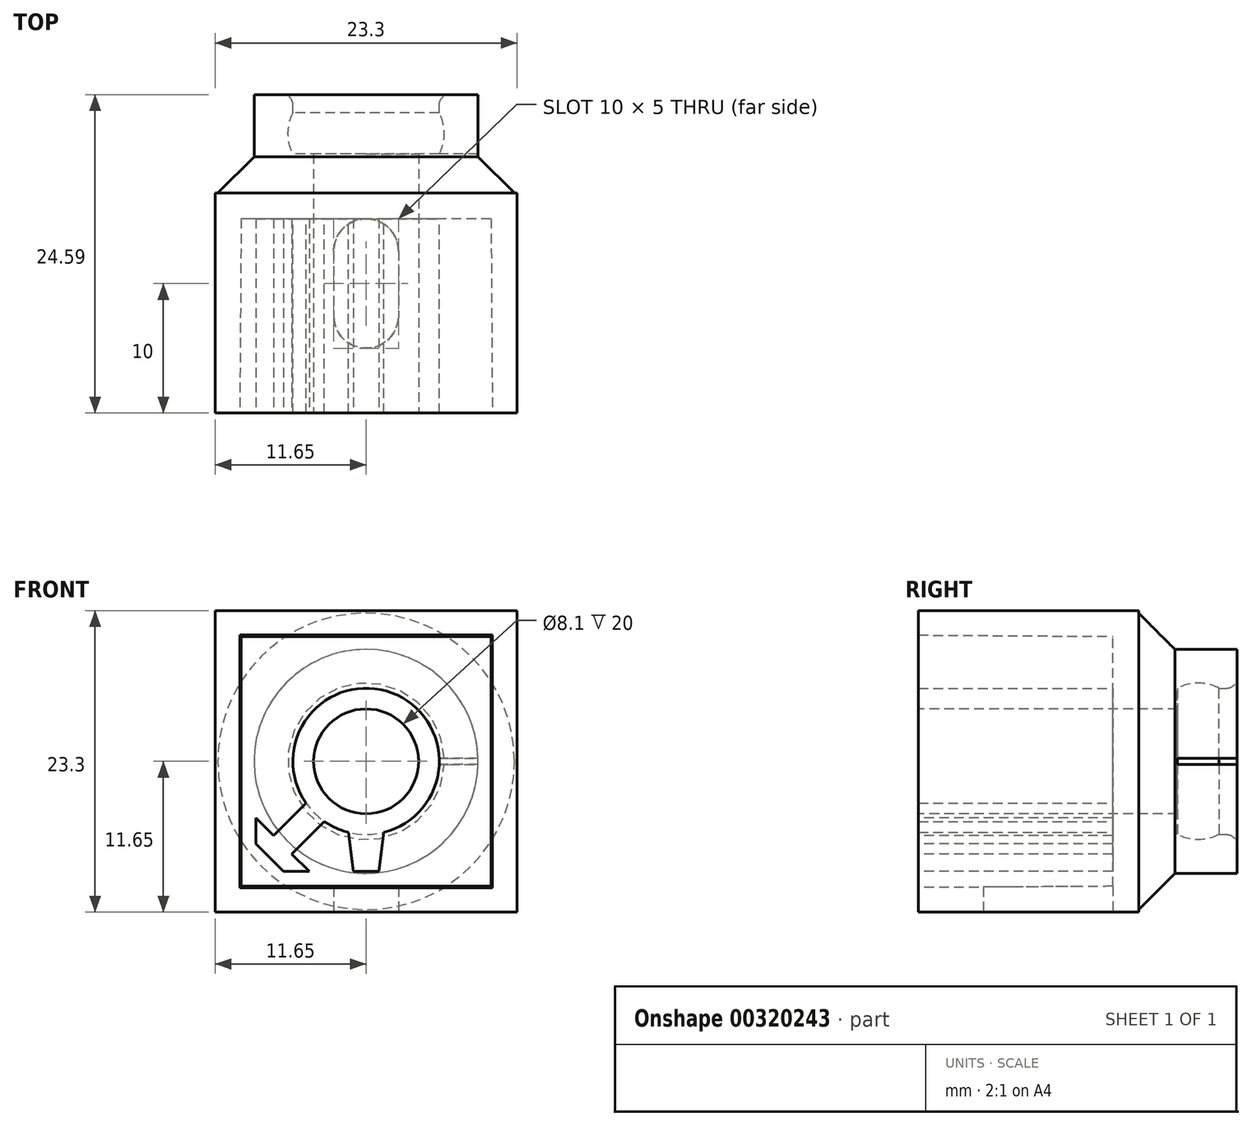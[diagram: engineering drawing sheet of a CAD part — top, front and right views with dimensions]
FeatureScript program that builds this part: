
annotation { "Feature Type Name" : "Feature", "Feature Type Description" : "" }
export const myFeature = defineFeature(function(context is Context, id is Id, definition is map)
    precondition{}
    {
        {
            var Q0;
            Q0=qCreatedBy(makeId("Front.planeOp"),FACE);
            var sketch = newSketch(context, id + "F0", { "sketchPlane" : qUnion([Q0])});
            skLineSegment(sketch, "E0.bottom", {"start": v(9.5, -9.5) * mm, "end": v(-9.5, -9.5) * mm, "construction": true});
            skLineSegment(sketch, "E0.top", {"start": v(9.5, 9.5) * mm, "end": v(-9.5, 9.5) * mm, "construction": true});
            skLineSegment(sketch, "E0.left", {"start": v(9.5, -9.5) * mm, "end": v(9.5, 9.5) * mm, "construction": true});
            skLineSegment(sketch, "E0.right", {"start": v(-9.5, -9.5) * mm, "end": v(-9.5, 9.5) * mm, "construction": true});
            skPoint(sketch, "E0.middle", {"position": v(0, 0) * mm});
            skLineSegment(sketch, "E1.0", {"start": v(8.5, 8.5) * mm, "end": v(-8.5, 8.5) * mm, "construction": true});
            skLineSegment(sketch, "E1.1", {"start": v(8.5, -8.5) * mm, "end": v(8.5, 8.5) * mm, "construction": true});
            skLineSegment(sketch, "E1.2", {"start": v(8.5, -8.5) * mm, "end": v(-8.5, -8.5) * mm, "construction": true});
            skLineSegment(sketch, "E1.3", {"start": v(-8.5, -8.5) * mm, "end": v(-8.5, 8.5) * mm, "construction": true});
            skSolve(sketch);
        }
        {
            var Q0;
            Q0=qCreatedBy(makeId("Front.planeOp"),FACE);
            var sketch = newSketch(context, id + "F1", { "sketchPlane" : qUnion([Q0])});
            skLineSegment(sketch, "E2.0", {"start": v(8.4, 8.4) * mm, "end": v(-8.4, 8.4) * mm});
            skLineSegment(sketch, "E2.1", {"start": v(8.4, -8.4) * mm, "end": v(8.4, 8.4) * mm});
            skLineSegment(sketch, "E2.2", {"start": v(8.4, -8.4) * mm, "end": v(-8.4, -8.4) * mm});
            skLineSegment(sketch, "E2.3", {"start": v(-8.4, -8.4) * mm, "end": v(-8.4, 8.4) * mm});
            skLineSegment(sketch, "E3.0", {"start": v(9.65, 9.65) * mm, "end": v(-9.65, 9.65) * mm});
            skLineSegment(sketch, "E3.1", {"start": v(9.65, -9.65) * mm, "end": v(9.65, 9.65) * mm});
            skLineSegment(sketch, "E3.2", {"start": v(9.65, -9.65) * mm, "end": v(-9.65, -9.65) * mm});
            skLineSegment(sketch, "E3.3", {"start": v(-9.65, -9.65) * mm, "end": v(-9.65, 9.65) * mm});
            skLineSegment(sketch, "E4.0", {"start": v(11.65, 11.65) * mm, "end": v(-11.65, 11.65) * mm});
            skLineSegment(sketch, "E4.1", {"start": v(11.65, -11.65) * mm, "end": v(11.65, 11.65) * mm});
            skLineSegment(sketch, "E4.2", {"start": v(11.65, -11.65) * mm, "end": v(-11.65, -11.65) * mm});
            skLineSegment(sketch, "E4.3", {"start": v(-11.65, -11.65) * mm, "end": v(-11.65, 11.65) * mm});
            skLineSegment(sketch, "E5.0", {"start": v(6.4, 6.4) * mm, "end": v(-6.4, 6.4) * mm});
            skLineSegment(sketch, "E5.1", {"start": v(6.4, -6.4) * mm, "end": v(6.4, 6.4) * mm});
            skLineSegment(sketch, "E5.2", {"start": v(6.4, -6.4) * mm, "end": v(-6.4, -6.4) * mm});
            skLineSegment(sketch, "E5.3", {"start": v(-6.4, -6.4) * mm, "end": v(-6.4, 6.4) * mm});
            skSolve(sketch);
        }
        {
            var Q0;
            Q0=makeQuery(id+"F1.imprint","IMPRINT",FACE,{"disambiguationData":[TD([[makeQuery(id+"F1.imprint","IMPRINT",EDGE,{"derivedFrom":sQuery(id+"F1.wireOp",EDGE,"E3.0")}),-1.0]])]});
            extrude(context, id + "F2", {"entities" : qUnion([Q0]), "oppositeDirection" : true, "depth" : 25 * mm});
        }
        {
            var Q0;
            Q0=makeQuery(id+"F2.opExtrude","CAP_FACE",FACE,{"disambiguationData":[OSD([sQuery(id+"F1.wireOp",EDGE,"E3.0"),sQuery(id+"F1.wireOp",EDGE,"E3.1"),sQuery(id+"F1.wireOp",EDGE,"E3.2"),sQuery(id+"F1.wireOp",EDGE,"E3.3"),sQuery(id+"F1.wireOp",EDGE,"E4.0"),sQuery(id+"F1.wireOp",EDGE,"E4.1"),sQuery(id+"F1.wireOp",EDGE,"E4.2"),sQuery(id+"F1.wireOp",EDGE,"E4.3")])],"isStart":true});
            var sketch = newSketch(context, id + "F3", { "sketchPlane" : qUnion([Q0])});
            skLineSegment(sketch, "E6.0.0", {"start": v(-11.65, 11.65) * mm, "end": v(-11.65, -11.65) * mm});
            skLineSegment(sketch, "E6.0.1", {"start": v(-11.65, -11.65) * mm, "end": v(11.65, -11.65) * mm});
            skLineSegment(sketch, "E6.0.2", {"start": v(11.65, -11.65) * mm, "end": v(11.65, 11.65) * mm});
            skLineSegment(sketch, "E6.0.3", {"start": v(11.65, 11.65) * mm, "end": v(-11.65, 11.65) * mm});
            skSolve(sketch);
        }
        {
            var Q0;
            Q0 = qSketchRegion(id + "F3", true);
            extrude(context, id + "F4", {"entities" : qUnion([Q0]), "operationType" : NewBodyOperationType.ADD, "oppositeDirection" : true, "depth" : 3 * mm});
        }
        {
            var Q0;
            Q0=makeQuery(id+"F4.boolean.opBoolean","MERGE",FACE,{"derivedFrom":[makeQuery(id+"F2.opExtrude","CAP_FACE",FACE,{"disambiguationData":[OSD([sQuery(id+"F1.wireOp",EDGE,"E2.0"),sQuery(id+"F1.wireOp",EDGE,"E2.1"),sQuery(id+"F1.wireOp",EDGE,"E2.2"),sQuery(id+"F1.wireOp",EDGE,"E2.3"),sQuery(id+"F1.wireOp",EDGE,"E5.0"),sQuery(id+"F1.wireOp",EDGE,"E5.1"),sQuery(id+"F1.wireOp",EDGE,"E5.2"),sQuery(id+"F1.wireOp",EDGE,"E5.3")])],"isStart":true}),makeQuery(id+"F2.opExtrude","CAP_FACE",FACE,{"disambiguationData":[OSD([sQuery(id+"F1.wireOp",EDGE,"E3.0"),sQuery(id+"F1.wireOp",EDGE,"E3.1"),sQuery(id+"F1.wireOp",EDGE,"E3.2"),sQuery(id+"F1.wireOp",EDGE,"E3.3"),sQuery(id+"F1.wireOp",EDGE,"E4.0"),sQuery(id+"F1.wireOp",EDGE,"E4.1"),sQuery(id+"F1.wireOp",EDGE,"E4.2"),sQuery(id+"F1.wireOp",EDGE,"E4.3")])],"isStart":true}),makeQuery(id+"F4.opExtrude","CAP_FACE",FACE,{"disambiguationData":[OSD([sQuery(id+"F3.wireOp",EDGE,"E6.0.0"),sQuery(id+"F3.wireOp",EDGE,"E6.0.1"),sQuery(id+"F3.wireOp",EDGE,"E6.0.2"),sQuery(id+"F3.wireOp",EDGE,"E6.0.3")])],"isStart":true})]});
            var sketch = newSketch(context, id + "F5", { "sketchPlane" : qUnion([Q0])});
            skCircle(sketch, "E7", {"center": v(0, 0) * mm, "radius": 4.05 * mm});
            skSolve(sketch);
        }
        {
            var Q0;
            Q0 = qSketchRegion(id + "F5", true);
            extrude(context, id + "F6", {"entities" : qUnion([Q0]), "operationType" : NewBodyOperationType.REMOVE, "endBound" : BoundingType.THROUGH_ALL, "oppositeDirection" : true, "depth" : 25 * mm});
        }
        {
            var Q0;
            Q0=qCreatedBy(makeId("Right.planeOp"),FACE);
            var sketch = newSketch(context, id + "F7", { "sketchPlane" : qUnion([Q0])});
            skLineSegment(sketch, "E8.bottom", {"start": v(3, -4.05) * mm, "end": v(20, -4.05) * mm});
            skLineSegment(sketch, "E8.top", {"start": v(3, -5.65) * mm, "end": v(20, -5.65) * mm});
            skLineSegment(sketch, "E8.left", {"start": v(3, -4.05) * mm, "end": v(3, -5.65) * mm});
            skLineSegment(sketch, "E8.right", {"start": v(20, -4.05) * mm, "end": v(20, -5.65) * mm});
            skArc(sketch, "E9", {"start": v(20, -5.65) * mm, "mid": v(21.6, -6.05) * mm, "end": v(23.2, -5.65) * mm});
            skLineSegment(sketch, "E10", {"start": v(23.2, -5.65) * mm, "end": v(26.09, -5.65) * mm});
            skArc(sketch, "E11.0", {"start": v(17.11, -5.65) * mm, "mid": v(21.6, -8.05) * mm, "end": v(26.09, -5.65) * mm});
            skLineSegment(sketch, "E12", {"start": v(24.82, -8.05) * mm, "end": v(16.07, -8.05) * mm, "construction": true});
            skSolve(sketch);
        }
        {
            var Q0;
            Q0 = qSketchRegion(id + "F7", true);
            var Q1;
            Q1=makeQuery(id+"F6.boolean.opBoolean","INTERSECT",EDGE,{"derivedFrom":[makeQuery(id+"F4.opExtrude","CAP_FACE",FACE,{"disambiguationData":[OSD([sQuery(id+"F3.wireOp",EDGE,"E6.0.0"),sQuery(id+"F3.wireOp",EDGE,"E6.0.1"),sQuery(id+"F3.wireOp",EDGE,"E6.0.2"),sQuery(id+"F3.wireOp",EDGE,"E6.0.3")])],"isStart":false}),makeQuery(id+"F6.opExtrude","SWEPT_FACE",FACE,{"disambiguationData":[OSD([sQuery(id+"F5.wireOp",EDGE,"E7")])]})]});
            revolve(context, id + "F8", {"operationType" : NewBodyOperationType.ADD, "entities" : qUnion([Q0]), "axis" : qUnion([Q1]), "revolveType" : RevolveType.FULL});
        }
        {
            var Q0;
            Q0=makeQuery(id+"F2.opExtrude","CAP_FACE",FACE,{"disambiguationData":[OSD([sQuery(id+"F1.wireOp",EDGE,"E3.0"),sQuery(id+"F1.wireOp",EDGE,"E3.1"),sQuery(id+"F1.wireOp",EDGE,"E3.2"),sQuery(id+"F1.wireOp",EDGE,"E3.3"),sQuery(id+"F1.wireOp",EDGE,"E4.0"),sQuery(id+"F1.wireOp",EDGE,"E4.1"),sQuery(id+"F1.wireOp",EDGE,"E4.2"),sQuery(id+"F1.wireOp",EDGE,"E4.3")])],"isStart":false});
            cPlane(context, id + "F9", {"entities" : qUnion([Q0]), "cplaneType" : CPlaneType.OFFSET, "offset" : 8 * mm, "oppositeDirection" : true, "width" : 150 * mm, "height" : 150 * mm});
        }
        {
            var Q0;
            Q0=qCreatedBy(id+"F9.planeOp",FACE);
            var sketch = newSketch(context, id + "F10", { "sketchPlane" : qUnion([Q0])});
            skLineSegment(sketch, "E13.0.0", {"start": v(11.65, -11.65) * mm, "end": v(11.65, 11.65) * mm});
            skLineSegment(sketch, "E13.0.1", {"start": v(11.65, 11.65) * mm, "end": v(-11.65, 11.65) * mm});
            skLineSegment(sketch, "E13.0.2", {"start": v(-11.65, 11.65) * mm, "end": v(-11.65, -11.65) * mm});
            skLineSegment(sketch, "E13.0.3", {"start": v(-11.65, -11.65) * mm, "end": v(11.65, -11.65) * mm});
            skSolve(sketch);
        }
        {
            var Q0;
            Q0 = qSketchRegion(id + "F10", true);
            extrude(context, id + "F11", {"entities" : qUnion([Q0]), "oppositeDirection" : true, "depth" : 2 * mm});
        }
        {
            var Q0;
            Q0=makeQuery(id+"F2.opExtrude","SWEPT_BODY",BODY,{"disambiguationData":[OSD([sQuery(id+"F1.wireOp",EDGE,"E3.0"),sQuery(id+"F1.wireOp",EDGE,"E3.1"),sQuery(id+"F1.wireOp",EDGE,"E3.2"),sQuery(id+"F1.wireOp",EDGE,"E3.3"),sQuery(id+"F1.wireOp",EDGE,"E4.0"),sQuery(id+"F1.wireOp",EDGE,"E4.1"),sQuery(id+"F1.wireOp",EDGE,"E4.2"),sQuery(id+"F1.wireOp",EDGE,"E4.3")])]});
            var Q1;
            Q1=makeQuery(id+"F11.opExtrude","SWEPT_BODY",BODY,{"disambiguationData":[OSD([sQuery(id+"F10.wireOp",EDGE,"E13.0.0"),sQuery(id+"F10.wireOp",EDGE,"E13.0.1"),sQuery(id+"F10.wireOp",EDGE,"E13.0.2"),sQuery(id+"F10.wireOp",EDGE,"E13.0.3")])]});
            booleanBodies(context, id + "F12", {"operationType" : BooleanOperationType.UNION, "tools" : qUnion([Q0, Q1])});
        }
        {
            var Q0;
            Q0=makeQuery(id+"F12.opBoolean","SPLIT",FACE,{"disambiguationData":[TD([makeQuery(id+"F6.boolean.opBoolean","COPY",FACE,{"derivedFrom":makeQuery(id+"F6.opExtrude","SWEPT_FACE",FACE,{"disambiguationData":[OSD([sQuery(id+"F5.wireOp",EDGE,"E7")])]})})])],"derivedFrom":makeQuery(id+"F11.opExtrude","CAP_FACE",FACE,{"disambiguationData":[OSD([sQuery(id+"F10.wireOp",EDGE,"E13.0.0"),sQuery(id+"F10.wireOp",EDGE,"E13.0.1"),sQuery(id+"F10.wireOp",EDGE,"E13.0.2"),sQuery(id+"F10.wireOp",EDGE,"E13.0.3")])],"isStart":true})});
            var sketch = newSketch(context, id + "F13", { "sketchPlane" : qUnion([Q0])});
            skCircle(sketch, "E14.0", {"center": v(0, 0) * mm, "radius": 4.05 * mm});
            skSolve(sketch);
        }
        {
            var Q0;
            Q0 = qSketchRegion(id + "F13", true);
            extrude(context, id + "F14", {"entities" : qUnion([Q0]), "operationType" : NewBodyOperationType.REMOVE, "endBound" : BoundingType.THROUGH_ALL, "oppositeDirection" : true, "depth" : 25 * mm});
        }
        {
            var Q0;
            Q0=makeQuery(id+"F4.opExtrude","CAP_FACE",FACE,{"disambiguationData":[OSD([sQuery(id+"F3.wireOp",EDGE,"E6.0.0"),sQuery(id+"F3.wireOp",EDGE,"E6.0.1"),sQuery(id+"F3.wireOp",EDGE,"E6.0.2"),sQuery(id+"F3.wireOp",EDGE,"E6.0.3")])],"isStart":false});
            var sketch = newSketch(context, id + "F15", { "sketchPlane" : qUnion([Q0])});
            skLineSegment(sketch, "E15.0.0", {"start": v(-9.65, -9.65) * mm, "end": v(9.65, -9.65) * mm});
            skLineSegment(sketch, "E15.0.1", {"start": v(9.65, -9.65) * mm, "end": v(9.65, 9.65) * mm});
            skLineSegment(sketch, "E15.0.2", {"start": v(9.65, 9.65) * mm, "end": v(-9.65, 9.65) * mm});
            skLineSegment(sketch, "E15.0.3", {"start": v(-9.65, 9.65) * mm, "end": v(-9.65, -9.65) * mm});
            skCircle(sketch, "E16.0", {"center": v(0, 0) * mm, "radius": 5.65 * mm});
            skSolve(sketch);
        }
        {
            var Q0;
            Q0 = qSketchRegion(id + "F15", true);
            extrude(context, id + "F16", {"entities" : qUnion([Q0]), "operationType" : NewBodyOperationType.REMOVE, "endBound" : BoundingType.THROUGH_ALL, "oppositeDirection" : true, "depth" : 25 * mm});
        }
        {
            var Q0;
            Q0=makeQuery(id+"F12.opBoolean","SPLIT",FACE,{"disambiguationData":[TD([makeQuery(id+"F2.opExtrude","SWEPT_FACE",FACE,{"disambiguationData":[OSD([sQuery(id+"F1.wireOp",EDGE,"E3.0")])]})])],"derivedFrom":makeQuery(id+"F11.opExtrude","CAP_FACE",FACE,{"disambiguationData":[OSD([sQuery(id+"F10.wireOp",EDGE,"E13.0.0"),sQuery(id+"F10.wireOp",EDGE,"E13.0.1"),sQuery(id+"F10.wireOp",EDGE,"E13.0.2"),sQuery(id+"F10.wireOp",EDGE,"E13.0.3")])],"isStart":false})});
            var sketch = newSketch(context, id + "F17", { "sketchPlane" : qUnion([Q0])});
            skLineSegment(sketch, "E17.0", {"start": v(9.5, -9.5) * mm, "end": v(-9.5, -9.5) * mm});
            skLineSegment(sketch, "E17.1", {"start": v(9.5, 9.5) * mm, "end": v(-9.5, 9.5) * mm});
            skLineSegment(sketch, "E17.2", {"start": v(9.5, -9.5) * mm, "end": v(9.5, 9.5) * mm});
            skLineSegment(sketch, "E17.3", {"start": v(-9.5, -9.5) * mm, "end": v(-9.5, 9.5) * mm});
            skPoint(sketch, "E17.4", {"position": v(0, 0) * mm});
            skLineSegment(sketch, "E17.5", {"start": v(8.5, 8.5) * mm, "end": v(-8.5, 8.5) * mm});
            skLineSegment(sketch, "E17.6", {"start": v(8.5, -8.5) * mm, "end": v(8.5, 8.5) * mm});
            skLineSegment(sketch, "E17.7", {"start": v(8.5, -8.5) * mm, "end": v(-8.5, -8.5) * mm});
            skLineSegment(sketch, "E17.8", {"start": v(-8.5, -8.5) * mm, "end": v(-8.5, 8.5) * mm});
            skSolve(sketch);
        }
        {
            var Q0;
            {var subQ0=sQuery(id+"F1.wireOp",EDGE,"E4.3");var subQ1=sQuery(id+"F1.wireOp",EDGE,"E4.2");var subQ2=sQuery(id+"F1.wireOp",EDGE,"E4.1");var subQ3=sQuery(id+"F1.wireOp",EDGE,"E4.0");var subQ4=sQuery(id+"F1.wireOp",EDGE,"E3.0");var subQ5=sQuery(id+"F1.wireOp",EDGE,"E3.3");var subQ6=sQuery(id+"F1.wireOp",EDGE,"E3.1");var subQ7=sQuery(id+"F1.wireOp",EDGE,"E3.2");Q0=makeQuery(id+"F16.boolean.opBoolean","SPLIT",FACE,{"disambiguationData":[TD([makeQuery(id+"F2.opExtrude","SWEPT_FACE",FACE,{"disambiguationData":[OSD([subQ4])]})])],"derivedFrom":makeQuery(id+"F4.boolean.opBoolean","MERGE",FACE,{"derivedFrom":[makeQuery(id+"F2.opExtrude","CAP_FACE",FACE,{"disambiguationData":[OSD([subQ4,subQ6,subQ7,subQ5,subQ3,subQ2,subQ1,subQ0])],"isStart":true}),makeQuery(id+"F4.opExtrude","CAP_FACE",FACE,{"disambiguationData":[OSD([sQuery(id+"F3.wireOp",EDGE,"E6.0.0"),sQuery(id+"F3.wireOp",EDGE,"E6.0.1"),sQuery(id+"F3.wireOp",EDGE,"E6.0.2"),sQuery(id+"F3.wireOp",EDGE,"E6.0.3")])],"isStart":true})]})});}
            var sketch = newSketch(context, id + "F18", { "sketchPlane" : qUnion([Q0])});
            skLineSegment(sketch, "E18", {"start": v(1.5, -4.5) * mm, "end": v(0.97, -8.5) * mm});
            skLineSegment(sketch, "E19", {"start": v(-0.97, -8.5) * mm, "end": v(-1.5, -4.5) * mm});
            skLineSegment(sketch, "E20", {"start": v(-1.5, -4.5) * mm, "end": v(1.5, -4.5) * mm});
            skLineSegment(sketch, "E21.0", {"start": v(8.5, -8.5) * mm, "end": v(-8.5, -8.5) * mm, "construction": true});
            skPoint(sketch, "E22.orphan", {"position": v(0, -15.9) * mm});
            skLineSegment(sketch, "E23", {"start": v(-0.97, -8.5) * mm, "end": v(0.97, -8.5) * mm});
            skSolve(sketch);
        }
        {
            var Q0;
            Q0 = qSketchRegion(id + "F18", true);
            var Q1;
            Q1=makeQuery(id+"F12.opBoolean","SPLIT",FACE,{"disambiguationData":[TD([makeQuery(id+"F2.opExtrude","SWEPT_FACE",FACE,{"disambiguationData":[OSD([sQuery(id+"F1.wireOp",EDGE,"E3.0")])]})])],"derivedFrom":makeQuery(id+"F11.opExtrude","CAP_FACE",FACE,{"disambiguationData":[OSD([sQuery(id+"F10.wireOp",EDGE,"E13.0.0"),sQuery(id+"F10.wireOp",EDGE,"E13.0.1"),sQuery(id+"F10.wireOp",EDGE,"E13.0.2"),sQuery(id+"F10.wireOp",EDGE,"E13.0.3")])],"isStart":false})});
            extrude(context, id + "F19", {"entities" : qUnion([Q0]), "operationType" : NewBodyOperationType.ADD, "endBound" : BoundingType.UP_TO_SURFACE, "oppositeDirection" : true, "endBoundEntityFace" : qUnion([Q1]), "depth" : 25 * mm});
        }
        {
            var Q0;
            {var subQ0=sQuery(id+"F1.wireOp",EDGE,"E4.3");var subQ1=sQuery(id+"F1.wireOp",EDGE,"E4.2");var subQ2=sQuery(id+"F1.wireOp",EDGE,"E4.1");var subQ3=sQuery(id+"F1.wireOp",EDGE,"E4.0");var subQ4=sQuery(id+"F1.wireOp",EDGE,"E3.0");var subQ5=sQuery(id+"F1.wireOp",EDGE,"E3.3");var subQ6=sQuery(id+"F1.wireOp",EDGE,"E3.1");var subQ7=sQuery(id+"F1.wireOp",EDGE,"E3.2");Q0=makeQuery(id+"F16.boolean.opBoolean","SPLIT",FACE,{"disambiguationData":[TD([makeQuery(id+"F2.opExtrude","SWEPT_FACE",FACE,{"disambiguationData":[OSD([subQ4])]})])],"derivedFrom":makeQuery(id+"F4.boolean.opBoolean","MERGE",FACE,{"derivedFrom":[makeQuery(id+"F2.opExtrude","CAP_FACE",FACE,{"disambiguationData":[OSD([subQ4,subQ6,subQ7,subQ5,subQ3,subQ2,subQ1,subQ0])],"isStart":true}),makeQuery(id+"F4.opExtrude","CAP_FACE",FACE,{"disambiguationData":[OSD([sQuery(id+"F3.wireOp",EDGE,"E6.0.0"),sQuery(id+"F3.wireOp",EDGE,"E6.0.1"),sQuery(id+"F3.wireOp",EDGE,"E6.0.2"),sQuery(id+"F3.wireOp",EDGE,"E6.0.3")])],"isStart":true})]})});}
            var sketch = newSketch(context, id + "F20", { "sketchPlane" : qUnion([Q0])});
            skLineSegment(sketch, "E24", {"start": v(-6.38, -8.5) * mm, "end": v(-8.5, -6.38) * mm});
            skLineSegment(sketch, "E25.0", {"start": v(-8.5, -6.38) * mm, "end": v(-8.5, -4.38) * mm});
            skLineSegment(sketch, "E26.0", {"start": v(-4.38, -8.5) * mm, "end": v(-6.38, -8.5) * mm});
            skCircle(sketch, "E27.0", {"center": v(0, 0) * mm, "radius": 4.05 * mm});
            skPoint(sketch, "E28.orphan", {"position": v(-8.5, 8.5) * mm});
            skPoint(sketch, "E29.orphan", {"position": v(8.5, -8.5) * mm});
            skPoint(sketch, "E30.orphan", {"position": v(-8.5, -8.5) * mm});
            skLineSegment(sketch, "E31", {"start": v(-8.5, -4.38) * mm, "end": v(-4.38, -8.5) * mm});
            skLineSegment(sketch, "E32", {"start": v(-6.44, -6.44) * mm, "end": v(0, 0) * mm, "construction": true});
            skLineSegment(sketch, "E33.0", {"start": v(-5.73, -7.15) * mm, "end": v(-2.07, -3.48) * mm});
            skLineSegment(sketch, "E34.0", {"start": v(-7.15, -5.73) * mm, "end": v(-3.48, -2.07) * mm});
            skSolve(sketch);
        }
        {
            var Q0;
            Q0=makeQuery(id+"F20.imprint","IMPRINT",FACE,{"disambiguationData":[TD([[makeQuery(id+"F20.imprint","IMPRINT",EDGE,{"derivedFrom":sQuery(id+"F20.wireOp",EDGE,"E24")}),-1.0]])]});
            var Q1;
            {var subQ0=sQuery(id+"F20.wireOp",EDGE,"E33.0");Q1=makeQuery(id+"F20.imprint","IMPRINT",FACE,{"disambiguationData":[TD([[makeQuery(id+"F20.imprint","IMPRINT",EDGE,{"derivedFrom":subQ0}),1.0]])]});}
            var Q2;
            Q2=makeQuery(id+"F12.opBoolean","SPLIT",FACE,{"disambiguationData":[TD([makeQuery(id+"F2.opExtrude","SWEPT_FACE",FACE,{"disambiguationData":[OSD([sQuery(id+"F1.wireOp",EDGE,"E3.0")])]})])],"derivedFrom":makeQuery(id+"F11.opExtrude","CAP_FACE",FACE,{"disambiguationData":[OSD([sQuery(id+"F10.wireOp",EDGE,"E13.0.0"),sQuery(id+"F10.wireOp",EDGE,"E13.0.1"),sQuery(id+"F10.wireOp",EDGE,"E13.0.2"),sQuery(id+"F10.wireOp",EDGE,"E13.0.3")])],"isStart":false})});
            extrude(context, id + "F21", {"entities" : qUnion([Q0, Q1]), "operationType" : NewBodyOperationType.ADD, "endBound" : BoundingType.UP_TO_SURFACE, "oppositeDirection" : true, "endBoundEntityFace" : qUnion([Q2]), "depth" : 25 * mm});
        }
        {
            var Q0;
            Q0=makeQuery(id+"F16.boolean.opBoolean","INTERSECT",EDGE,{"derivedFrom":[makeQuery(id+"F4.boolean.opBoolean","MERGE",FACE,{"derivedFrom":[makeQuery(id+"F2.opExtrude","CAP_FACE",FACE,{"disambiguationData":[OSD([sQuery(id+"F1.wireOp",EDGE,"E3.0"),sQuery(id+"F1.wireOp",EDGE,"E3.1"),sQuery(id+"F1.wireOp",EDGE,"E3.2"),sQuery(id+"F1.wireOp",EDGE,"E3.3"),sQuery(id+"F1.wireOp",EDGE,"E4.0"),sQuery(id+"F1.wireOp",EDGE,"E4.1"),sQuery(id+"F1.wireOp",EDGE,"E4.2"),sQuery(id+"F1.wireOp",EDGE,"E4.3")])],"isStart":true}),makeQuery(id+"F4.opExtrude","CAP_FACE",FACE,{"disambiguationData":[OSD([sQuery(id+"F3.wireOp",EDGE,"E6.0.0"),sQuery(id+"F3.wireOp",EDGE,"E6.0.1"),sQuery(id+"F3.wireOp",EDGE,"E6.0.2"),sQuery(id+"F3.wireOp",EDGE,"E6.0.3")])],"isStart":true})]}),makeQuery(id+"F16.opExtrude","SWEPT_FACE",FACE,{"disambiguationData":[OSD([sQuery(id+"F15.wireOp",EDGE,"E15.0.0")])]})]});
            var Q1;
            Q1=makeQuery(id+"F16.boolean.opBoolean","INTERSECT",EDGE,{"derivedFrom":[makeQuery(id+"F4.boolean.opBoolean","MERGE",FACE,{"derivedFrom":[makeQuery(id+"F2.opExtrude","CAP_FACE",FACE,{"disambiguationData":[OSD([sQuery(id+"F1.wireOp",EDGE,"E3.0"),sQuery(id+"F1.wireOp",EDGE,"E3.1"),sQuery(id+"F1.wireOp",EDGE,"E3.2"),sQuery(id+"F1.wireOp",EDGE,"E3.3"),sQuery(id+"F1.wireOp",EDGE,"E4.0"),sQuery(id+"F1.wireOp",EDGE,"E4.1"),sQuery(id+"F1.wireOp",EDGE,"E4.2"),sQuery(id+"F1.wireOp",EDGE,"E4.3")])],"isStart":true}),makeQuery(id+"F4.opExtrude","CAP_FACE",FACE,{"disambiguationData":[OSD([sQuery(id+"F3.wireOp",EDGE,"E6.0.0"),sQuery(id+"F3.wireOp",EDGE,"E6.0.1"),sQuery(id+"F3.wireOp",EDGE,"E6.0.2"),sQuery(id+"F3.wireOp",EDGE,"E6.0.3")])],"isStart":true})]}),makeQuery(id+"F16.opExtrude","SWEPT_FACE",FACE,{"disambiguationData":[OSD([sQuery(id+"F15.wireOp",EDGE,"E15.0.3")])]})]});
            var Q2;
            Q2=makeQuery(id+"F16.boolean.opBoolean","INTERSECT",EDGE,{"derivedFrom":[makeQuery(id+"F4.boolean.opBoolean","MERGE",FACE,{"derivedFrom":[makeQuery(id+"F2.opExtrude","CAP_FACE",FACE,{"disambiguationData":[OSD([sQuery(id+"F1.wireOp",EDGE,"E3.0"),sQuery(id+"F1.wireOp",EDGE,"E3.1"),sQuery(id+"F1.wireOp",EDGE,"E3.2"),sQuery(id+"F1.wireOp",EDGE,"E3.3"),sQuery(id+"F1.wireOp",EDGE,"E4.0"),sQuery(id+"F1.wireOp",EDGE,"E4.1"),sQuery(id+"F1.wireOp",EDGE,"E4.2"),sQuery(id+"F1.wireOp",EDGE,"E4.3")])],"isStart":true}),makeQuery(id+"F4.opExtrude","CAP_FACE",FACE,{"disambiguationData":[OSD([sQuery(id+"F3.wireOp",EDGE,"E6.0.0"),sQuery(id+"F3.wireOp",EDGE,"E6.0.1"),sQuery(id+"F3.wireOp",EDGE,"E6.0.2"),sQuery(id+"F3.wireOp",EDGE,"E6.0.3")])],"isStart":true})]}),makeQuery(id+"F16.opExtrude","SWEPT_FACE",FACE,{"disambiguationData":[OSD([sQuery(id+"F15.wireOp",EDGE,"E15.0.1")])]})]});
            var Q3;
            Q3=makeQuery(id+"F16.boolean.opBoolean","INTERSECT",EDGE,{"derivedFrom":[makeQuery(id+"F4.boolean.opBoolean","MERGE",FACE,{"derivedFrom":[makeQuery(id+"F2.opExtrude","CAP_FACE",FACE,{"disambiguationData":[OSD([sQuery(id+"F1.wireOp",EDGE,"E3.0"),sQuery(id+"F1.wireOp",EDGE,"E3.1"),sQuery(id+"F1.wireOp",EDGE,"E3.2"),sQuery(id+"F1.wireOp",EDGE,"E3.3"),sQuery(id+"F1.wireOp",EDGE,"E4.0"),sQuery(id+"F1.wireOp",EDGE,"E4.1"),sQuery(id+"F1.wireOp",EDGE,"E4.2"),sQuery(id+"F1.wireOp",EDGE,"E4.3")])],"isStart":true}),makeQuery(id+"F4.opExtrude","CAP_FACE",FACE,{"disambiguationData":[OSD([sQuery(id+"F3.wireOp",EDGE,"E6.0.0"),sQuery(id+"F3.wireOp",EDGE,"E6.0.1"),sQuery(id+"F3.wireOp",EDGE,"E6.0.2"),sQuery(id+"F3.wireOp",EDGE,"E6.0.3")])],"isStart":true})]}),makeQuery(id+"F16.opExtrude","SWEPT_FACE",FACE,{"disambiguationData":[OSD([sQuery(id+"F15.wireOp",EDGE,"E15.0.2")])]})]});
            chamfer(context, id + "F22", {"entities" : qUnion([Q0, Q1, Q2, Q3]), "chamferType" : ChamferType.TWO_OFFSETS, "width1" : .1 * mm, "oppositeDirection" : false, "width2" : 15 * mm, "tangentPropagation" : true});
        }
        {
            var Q0;
            Q0=makeQuery(id+"F2.opExtrude","SWEPT_FACE",FACE,{"disambiguationData":[OSD([sQuery(id+"F1.wireOp",EDGE,"E4.2")])]});
            var sketch = newSketch(context, id + "F23", { "sketchPlane" : qUnion([Q0])});
            skLineSegment(sketch, "E35.bottom", {"start": v(2.5, -15) * mm, "end": v(-2.5, -15) * mm});
            skLineSegment(sketch, "E35.top", {"start": v(2.5, -5) * mm, "end": v(-2.5, -5) * mm});
            skLineSegment(sketch, "E35.left", {"start": v(2.5, -15) * mm, "end": v(2.5, -5) * mm});
            skLineSegment(sketch, "E35.right", {"start": v(-2.5, -15) * mm, "end": v(-2.5, -5) * mm});
            skPoint(sketch, "E35.middle", {"position": v(0, -10) * mm});
            skSolve(sketch);
        }
        {
            var Q0;
            Q0 = qSketchRegion(id + "F23", true);
            extrude(context, id + "F24", {"entities" : qUnion([Q0]), "operationType" : NewBodyOperationType.REMOVE, "oppositeDirection" : true, "depth" : 2.5 * mm});
        }
        {
            var Q0;
            Q0=makeQuery(id+"F24.boolean.opBoolean","COPY",EDGE,{"derivedFrom":makeQuery(id+"F24.opExtrude","SWEPT_EDGE",EDGE,{"disambiguationData":[OSD([sQuery(id+"F23.wireOp",EDGE,"E35.top"),sQuery(id+"F23.wireOp",EDGE,"E35.right")])]})});
            var Q1;
            Q1=makeQuery(id+"F24.boolean.opBoolean","COPY",EDGE,{"derivedFrom":makeQuery(id+"F24.opExtrude","SWEPT_EDGE",EDGE,{"disambiguationData":[OSD([sQuery(id+"F23.wireOp",EDGE,"E35.top"),sQuery(id+"F23.wireOp",EDGE,"E35.left")])]})});
            var Q2;
            Q2=makeQuery(id+"F24.boolean.opBoolean","COPY",EDGE,{"derivedFrom":makeQuery(id+"F24.opExtrude","SWEPT_EDGE",EDGE,{"disambiguationData":[OSD([sQuery(id+"F23.wireOp",EDGE,"E35.bottom"),sQuery(id+"F23.wireOp",EDGE,"E35.right")])]})});
            var Q3;
            Q3=makeQuery(id+"F24.boolean.opBoolean","COPY",EDGE,{"derivedFrom":makeQuery(id+"F24.opExtrude","SWEPT_EDGE",EDGE,{"disambiguationData":[OSD([sQuery(id+"F23.wireOp",EDGE,"E35.bottom"),sQuery(id+"F23.wireOp",EDGE,"E35.left")])]})});
            fillet(context, id + "F25", {"entities" : qUnion([Q0, Q1, Q2, Q3]), "radius" : 2.5 * mm, "tangentPropagation" : true, "allowEdgeOverflow" : false});
        }
        {
            var Q0;
            Q0=makeQuery(id+"F2.opExtrude","CAP_FACE",FACE,{"disambiguationData":[OSD([sQuery(id+"F1.wireOp",EDGE,"E3.0"),sQuery(id+"F1.wireOp",EDGE,"E3.1"),sQuery(id+"F1.wireOp",EDGE,"E3.2"),sQuery(id+"F1.wireOp",EDGE,"E3.3"),sQuery(id+"F1.wireOp",EDGE,"E4.0"),sQuery(id+"F1.wireOp",EDGE,"E4.1"),sQuery(id+"F1.wireOp",EDGE,"E4.2"),sQuery(id+"F1.wireOp",EDGE,"E4.3")])],"isStart":false});
            var sketch = newSketch(context, id + "F26", { "sketchPlane" : qUnion([Q0])});
            skLineSegment(sketch, "E36.0.0", {"start": v(11.65, -11.65) * mm, "end": v(11.65, 11.65) * mm});
            skLineSegment(sketch, "E36.0.1", {"start": v(11.65, 11.65) * mm, "end": v(-11.65, 11.65) * mm});
            skLineSegment(sketch, "E36.0.2", {"start": v(-11.65, 11.65) * mm, "end": v(-11.65, -11.65) * mm});
            skLineSegment(sketch, "E36.0.3", {"start": v(-11.65, -11.65) * mm, "end": v(11.65, -11.65) * mm});
            skLineSegment(sketch, "E37.0", {"start": v(-9.65, -9.65) * mm, "end": v(9.65, -9.65) * mm});
            skLineSegment(sketch, "E38.0", {"start": v(-9.65, -9.65) * mm, "end": v(-9.65, 9.65) * mm});
            skLineSegment(sketch, "E39.0", {"start": v(-9.65, 9.65) * mm, "end": v(9.65, 9.65) * mm});
            skLineSegment(sketch, "E40.0", {"start": v(9.65, -9.65) * mm, "end": v(9.65, 9.65) * mm});
            skSolve(sketch);
        }
        {
            var Q0;
            Q0 = qSketchRegion(id + "F26", true);
            var Q1;
            Q1=makeQuery(id+"F12.opBoolean","SPLIT",FACE,{"disambiguationData":[TD([makeQuery(id+"F2.opExtrude","SWEPT_FACE",FACE,{"disambiguationData":[OSD([sQuery(id+"F1.wireOp",EDGE,"E3.0")])]})])],"derivedFrom":makeQuery(id+"F11.opExtrude","CAP_FACE",FACE,{"disambiguationData":[OSD([sQuery(id+"F10.wireOp",EDGE,"E13.0.0"),sQuery(id+"F10.wireOp",EDGE,"E13.0.1"),sQuery(id+"F10.wireOp",EDGE,"E13.0.2"),sQuery(id+"F10.wireOp",EDGE,"E13.0.3")])],"isStart":true})});
            extrude(context, id + "F27", {"entities" : qUnion([Q0]), "operationType" : NewBodyOperationType.REMOVE, "endBound" : BoundingType.UP_TO_SURFACE, "oppositeDirection" : true, "endBoundEntityFace" : qUnion([Q1]), "depth" : 25 * mm});
        }
        {
            var Q0;
            Q0=qCreatedBy(makeId("Right.planeOp"),FACE);
            var sketch = newSketch(context, id + "F28", { "sketchPlane" : qUnion([Q0])});
            skLineSegment(sketch, "E41.0", {"start": v(16.09, -4.05) * mm, "end": v(20, -4.05) * mm});
            skLineSegment(sketch, "E41.3", {"start": v(20, -4.05) * mm, "end": v(20, -5.65) * mm});
            skArc(sketch, "E41.4", {"start": v(20, -5.65) * mm, "mid": v(21.6, -6.05) * mm, "end": v(23.2, -5.65) * mm});
            skLineSegment(sketch, "E41.5", {"start": v(23.2, -5.65) * mm, "end": v(26.09, -5.65) * mm});
            skLineSegment(sketch, "E41.7", {"start": v(24.82, -8.05) * mm, "end": v(16.07, -8.05) * mm, "construction": true});
            skLineSegment(sketch, "E42", {"start": v(26.09, -5.65) * mm, "end": v(26.09, -8.65) * mm});
            skLineSegment(sketch, "E43", {"start": v(26.09, -8.65) * mm, "end": v(16.09, -8.65) * mm});
            skLineSegment(sketch, "E44", {"start": v(16.09, -8.65) * mm, "end": v(16.09, -4.05) * mm});
            skPoint(sketch, "E45.orphan", {"position": v(3, -4.05) * mm});
            skSolve(sketch);
        }
        {
            var Q0;
            Q0 = qSketchRegion(id + "F28", true);
            var Q1;
            Q1=makeQuery(id+"F8.opRevolve","SWEPT_EDGE",EDGE,{"disambiguationData":[OSD([sQuery(id+"F7.wireOp",EDGE,"E8.bottom"),sQuery(id+"F7.wireOp",EDGE,"E8.right")])]});
            revolve(context, id + "F29", {"operationType" : NewBodyOperationType.ADD, "entities" : qUnion([Q0]), "axis" : qUnion([Q1]), "revolveType" : RevolveType.FULL});
        }
        {
            var Q0;
            {var subQ0=sQuery(id+"F10.wireOp",EDGE,"E13.0.3");var subQ1=sQuery(id+"F10.wireOp",EDGE,"E13.0.2");var subQ2=sQuery(id+"F10.wireOp",EDGE,"E13.0.1");var subQ3=sQuery(id+"F10.wireOp",EDGE,"E13.0.0");Q0=makeQuery(id+"F29.boolean.opBoolean","INTERSECT",EDGE,{"derivedFrom":[makeQuery(id+"F27.boolean.opBoolean","MERGE",FACE,{"derivedFrom":[makeQuery(id+"F12.opBoolean","SPLIT",FACE,{"disambiguationData":[TD([makeQuery(id+"F2.opExtrude","SWEPT_FACE",FACE,{"disambiguationData":[OSD([sQuery(id+"F1.wireOp",EDGE,"E3.0")])]})])],"derivedFrom":makeQuery(id+"F11.opExtrude","CAP_FACE",FACE,{"disambiguationData":[OSD([subQ3,subQ2,subQ1,subQ0])],"isStart":true})}),makeQuery(id+"F27.opExtrude","CAP_FACE",FACE,{"disambiguationData":[OSD([subQ3,subQ2,subQ1,subQ0])],"isStart":false})]}),makeQuery(id+"F29.opRevolve","SWEPT_FACE",FACE,{"disambiguationData":[OSD([sQuery(id+"F28.wireOp",EDGE,"E43")])]})]});}
            chamfer(context, id + "F30", {"entities" : qUnion([Q0]), "chamferType" : ChamferType.OFFSET_ANGLE, "width" : 2.8 * mm, "oppositeDirection" : false, "angle" : 45 * degree, "tangentPropagation" : true});
        }
        {
            var Q0;
            Q0=makeQuery(id+"F29.opRevolve","SWEPT_FACE",FACE,{"disambiguationData":[OSD([sQuery(id+"F28.wireOp",EDGE,"E42")])]});
            var sketch = newSketch(context, id + "F31", { "sketchPlane" : qUnion([Q0])});
            skCircle(sketch, "E46.0.0", {"center": v(0, 0) * mm, "radius": 8.65 * mm});
            skSolve(sketch);
        }
        {
            var Q0;
            Q0=makeQuery(id+"F31.imprint","IMPRINT",FACE,{"disambiguationData":[TD([[makeQuery(id+"F31.imprint","IMPRINT",EDGE,{"derivedFrom":sQuery(id+"F31.wireOp",EDGE,"E46.0.0")}),-1.0]])]});
            var Q1;
            Q1=makeQuery(id+"F31.imprint","IMPRINT",FACE,{"disambiguationData":[TD([[makeQuery(id+"F31.imprint","IMPRINT",EDGE,{"derivedFrom":makeQuery(id+"F29.boolean.opBoolean","MERGE",EDGE,{"derivedFrom":[makeQuery(id+"F8.opRevolve","SWEPT_EDGE",EDGE,{"disambiguationData":[OSD([sQuery(id+"F7.wireOp",EDGE,"E10"),sQuery(id+"F7.wireOp",EDGE,"E11.0")])]}),makeQuery(id+"F29.opRevolve","SWEPT_EDGE",EDGE,{"disambiguationData":[OSD([sQuery(id+"F28.wireOp",EDGE,"E41.5"),sQuery(id+"F28.wireOp",EDGE,"E42")])]})]})}),-1.0]])]});
            extrude(context, id + "F32", {"entities" : qUnion([Q0, Q1]), "operationType" : NewBodyOperationType.REMOVE, "oppositeDirection" : true, "depth" : 1.5 * mm});
        }
        {
            var Q0;
            Q0=makeQuery(id+"F29.boolean.opBoolean","MERGE",EDGE,{"derivedFrom":[makeQuery(id+"F8.opRevolve","SWEPT_EDGE",EDGE,{"disambiguationData":[OSD([sQuery(id+"F7.wireOp",EDGE,"E10"),sQuery(id+"F7.wireOp",EDGE,"E11.0")])]}),makeQuery(id+"F29.opRevolve","SWEPT_EDGE",EDGE,{"disambiguationData":[OSD([sQuery(id+"F28.wireOp",EDGE,"E41.5"),sQuery(id+"F28.wireOp",EDGE,"E42")])]})]});
            var Q1;
            Q1=makeQuery(id+"F32.boolean.opBoolean","INTERSECT",EDGE,{"derivedFrom":[makeQuery(id+"F8.opRevolve","SWEPT_FACE",FACE,{"disambiguationData":[OSD([sQuery(id+"F7.wireOp",EDGE,"E10")])]}),makeQuery(id+"F32.opExtrude","CAP_FACE",FACE,{"disambiguationData":[OSD([sQuery(id+"F31.wireOp",EDGE,"E46.0.0")])],"isStart":false})]});
            fillet(context, id + "F33", {"entities" : qUnion([Q0, Q1]), "radius" : .8 * mm, "tangentPropagation" : true, "allowEdgeOverflow" : false});
        }
        {
            var Q0;
            Q0=makeQuery(id+"F32.boolean.opBoolean","COPY",FACE,{"derivedFrom":makeQuery(id+"F32.opExtrude","CAP_FACE",FACE,{"disambiguationData":[OSD([sQuery(id+"F31.wireOp",EDGE,"E46.0.0")])],"isStart":false})});
            var sketch = newSketch(context, id + "F34", { "sketchPlane" : qUnion([Q0])});
            skLineSegment(sketch, "E47.bottom", {"start": v(-5, 0.25) * mm, "end": v(-15, 0.25) * mm});
            skLineSegment(sketch, "E47.top", {"start": v(-5, -0.25) * mm, "end": v(-15, -0.25) * mm});
            skLineSegment(sketch, "E47.left", {"start": v(-5, 0.25) * mm, "end": v(-5, -0.25) * mm});
            skLineSegment(sketch, "E47.right", {"start": v(-15, 0.25) * mm, "end": v(-15, -0.25) * mm});
            skPoint(sketch, "E47.middle", {"position": v(-10, 0) * mm});
            skSolve(sketch);
        }
        {
            var Q0;
            Q0 = qSketchRegion(id + "F34", true);
            var Q1;
            Q1=makeQuery(id+"F8.opRevolve","SWEPT_FACE",FACE,{"disambiguationData":[OSD([sQuery(id+"F7.wireOp",EDGE,"E8.right")])]});
            extrude(context, id + "F35", {"entities" : qUnion([Q0]), "operationType" : NewBodyOperationType.REMOVE, "endBound" : BoundingType.UP_TO_SURFACE, "oppositeDirection" : true, "endBoundEntityFace" : qUnion([Q1]), "depth" : 25 * mm});
        }
    });
